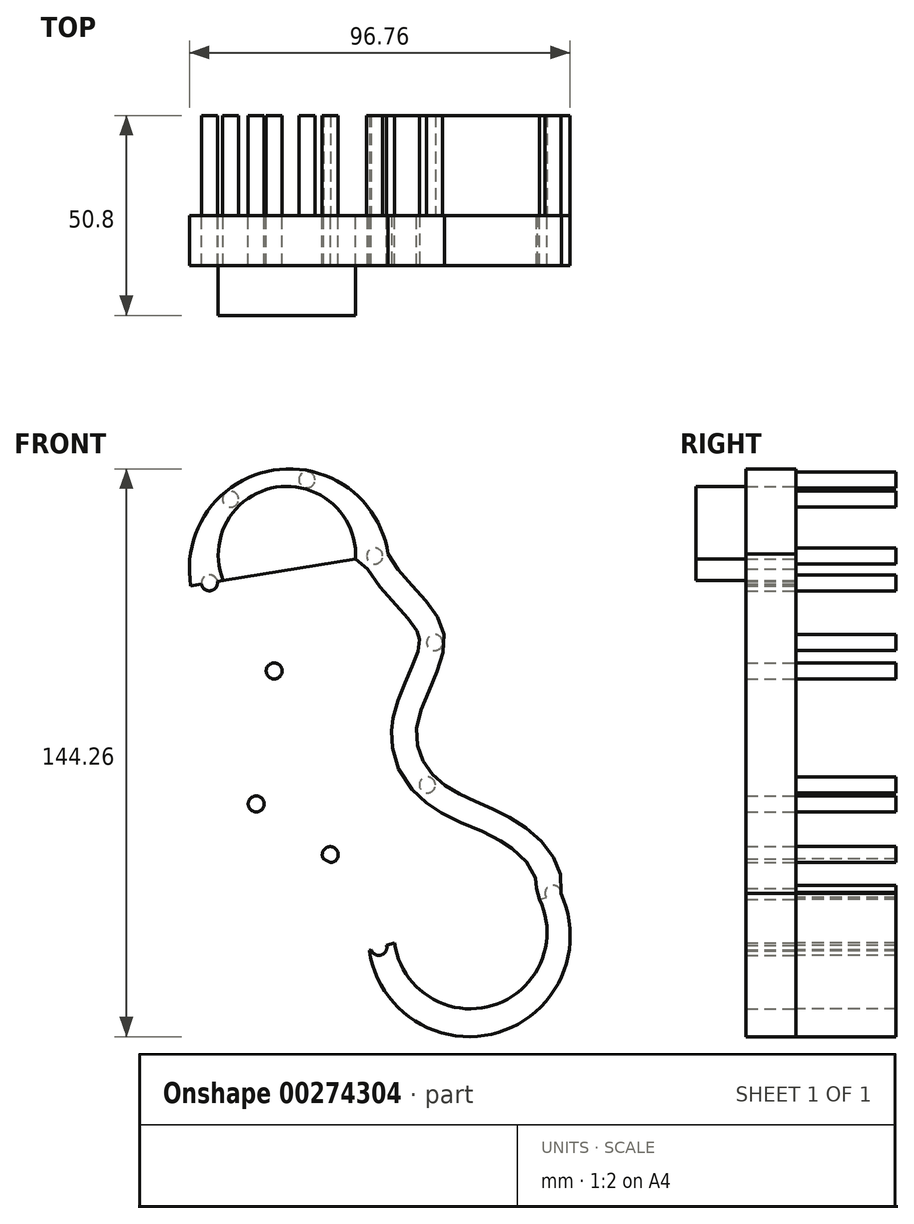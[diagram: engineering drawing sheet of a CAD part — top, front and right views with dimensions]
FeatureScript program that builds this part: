
annotation { "Feature Type Name" : "Feature", "Feature Type Description" : "" }
export const myFeature = defineFeature(function(context is Context, id is Id, definition is map)
    precondition{}
    {
        {
            var Q0;
            Q0=qCreatedBy(makeId("Front.planeOp"),FACE);
            var sketch = newSketch(context, id + "F0", { "sketchPlane" : qUnion([Q0])});
            skLineSegment(sketch, "E0", {"start": v(-45.2, 59.94) * mm, "end": v(4.95, 68.07) * mm});
            skArc(sketch, "E1", {"start": v(4.95, 68.07) * mm, "mid": v(-24.22, 89.33) * mm, "end": v(-45.2, 59.94) * mm});
            skLineSegment(sketch, "E2", {"start": v(0.14, -32.66) * mm, "end": v(48.83, -18.16) * mm});
            skFitSpline(sketch, "E3", {"points": [v(48.83, -18.16) * mm, v(37.71, 0) * mm, v(19, 9.5) * mm, v(12.27, 24.35) * mm, v(19.1, 47.9) * mm, v(4.95, 68.07) * mm], "startDerivative": vector(21.83, 107.44) * mm, "endDerivative": vector(-42.64, 94.14) * mm});
            skArc(sketch, "E4", {"start": v(0.14, -32.66) * mm, "mid": v(32.86, -53.53) * mm, "end": v(48.83, -18.16) * mm});
            skFitSpline(sketch, "E5.0", {"points": [v(-45.21, 59.96) * mm, v(-44.08, 58.98) * mm, v(-41.8, 57.02) * mm, v(-38.45, 54.02) * mm, v(-35.25, 50.94) * mm, v(-32.33, 47.77) * mm, v(-30.2, 45) * mm, v(-28.77, 42.66) * mm, v(-27.85, 40.83) * mm, v(-27.23, 39.23) * mm, v(-26.84, 37.9) * mm, v(-26.53, 36.55) * mm, v(-26.31, 34.87) * mm, v(-26.29, 32.9) * mm, v(-26.46, 30.99) * mm, v(-26.88, 28.53) * mm, v(-27.69, 25.6) * mm, v(-28.86, 22.23) * mm, v(-29.87, 19.47) * mm, v(-30.6, 17.28) * mm, v(-31.28, 15.1) * mm, v(-31.98, 12.3) * mm, v(-32.49, 9.06) * mm, v(-32.56, 6.55) * mm, v(-32.38, 4.74) * mm, v(-32.14, 3.5) * mm, v(-31.79, 2.38) * mm, v(-31.4, 1.55) * mm, v(-31.04, 0.93) * mm, v(-30.73, 0.49) * mm, v(-30.4, 0.06) * mm, v(-29.89, -0.48) * mm, v(-29.08, -1.19) * mm, v(-27.86, -2.05) * mm, v(-26.4, -2.9) * mm, v(-24.2, -4.02) * mm, v(-21.05, -5.38) * mm, v(-16.95, -7) * mm, v(-13.48, -8.46) * mm, v(-10.78, -9.8) * mm, v(-8.81, -10.9) * mm, v(-7.25, -11.96) * mm, v(-6.06, -12.9) * mm, v(-5.34, -13.55) * mm, v(-4.8, -14.1) * mm, v(-4.27, -14.66) * mm, v(-3.66, -15.39) * mm, v(-3, -16.3) * mm, v(-2.22, -17.54) * mm, v(-1.42, -19.16) * mm, v(-0.71, -21.15) * mm, v(-0.23, -23.16) * mm, v(0.17, -25.83) * mm, v(0.3, -29.16) * mm, v(0.14, -33.07) * mm, v(-0.07, -35.6) * mm, v(-0.17, -36.84) * mm]});
            skLineSegment(sketch, "E6", {"start": v(35.15, -22.23) * mm, "end": v(15.07, -28.21) * mm});
            skFitSpline(sketch, "E7.0", {"points": [v(42.6, -16.9) * mm, v(42.65, -16.66) * mm, v(42.7, -16.2) * mm, v(42.69, -15.5) * mm, v(42.56, -14.72) * mm, v(42.2, -13.58) * mm, v(41.39, -11.96) * mm, v(39.8, -9.87) * mm, v(38.05, -8.16) * mm, v(36.5, -6.88) * mm, v(35.47, -6.13) * mm, v(34.63, -5.57) * mm, v(33.8, -5.03) * mm, v(32.28, -4.15) * mm, v(29.98, -3) * mm, v(27.05, -1.72) * mm, v(23.96, -0.42) * mm, v(21.28, 0.78) * mm, v(19.1, 1.9) * mm, v(17.47, 2.84) * mm, v(15.84, 3.9) * mm, v(14.24, 5.13) * mm, v(12.73, 6.47) * mm, v(10.86, 8.44) * mm, v(8.8, 11.2) * mm, v(7.23, 14.39) * mm, v(6.36, 17.16) * mm, v(5.93, 19.34) * mm, v(5.76, 21.21) * mm, v(5.76, 22.74) * mm, v(5.82, 23.9) * mm, v(5.92, 24.87) * mm, v(6.04, 25.65) * mm, v(6.25, 26.8) * mm, v(6.65, 28.45) * mm, v(7.32, 30.53) * mm, v(8.08, 32.51) * mm, v(8.88, 34.41) * mm, v(9.68, 36.23) * mm, v(10.46, 37.97) * mm, v(11.17, 39.63) * mm, v(11.8, 41.18) * mm, v(12.3, 42.62) * mm, v(12.66, 43.9) * mm, v(12.87, 45.02) * mm, v(12.92, 45.78) * mm, v(12.91, 46.28) * mm, v(12.88, 46.6) * mm, v(12.83, 46.9) * mm, v(12.75, 47.22) * mm, v(12.62, 47.58) * mm, v(12.4, 48.12) * mm, v(12, 48.9) * mm, v(11.3, 49.98) * mm, v(10.4, 51.16) * mm, v(9.35, 52.42) * mm, v(8.17, 53.75) * mm, v(6.46, 55.6) * mm, v(4.17, 58.07) * mm, v(1.9, 60.82) * mm, v(0.24, 63.33) * mm, v(-0.5, 64.71) * mm, v(-0.83, 65.45) * mm]});
            skFitSpline(sketch, "E8.0", {"points": [v(-41.07, 64.76) * mm, v(-39.94, 63.8) * mm, v(-37.63, 61.8) * mm, v(-34.15, 58.69) * mm, v(-31.3, 55.96) * mm, v(-29.1, 53.65) * mm, v(-27.52, 51.84) * mm, v(-26, 49.95) * mm, v(-24.56, 47.93) * mm, v(-23.23, 45.77) * mm, v(-22.24, 43.82) * mm, v(-21.55, 42.16) * mm, v(-21.09, 40.87) * mm, v(-20.69, 39.51) * mm, v(-20.37, 38.1) * mm, v(-20.14, 36.7) * mm, v(-19.96, 34.86) * mm, v(-19.93, 32.65) * mm, v(-20.15, 30.15) * mm, v(-20.55, 27.85) * mm, v(-21.07, 25.7) * mm, v(-21.65, 23.7) * mm, v(-22.27, 21.85) * mm, v(-22.9, 20.09) * mm, v(-23.5, 18.42) * mm, v(-24.06, 16.84) * mm, v(-24.56, 15.33) * mm, v(-25.01, 13.87) * mm, v(-25.4, 12.44) * mm, v(-25.72, 11.04) * mm, v(-25.95, 9.71) * mm, v(-26.1, 8.48) * mm, v(-26.18, 7.37) * mm, v(-26.16, 6.41) * mm, v(-26.09, 5.63) * mm, v(-25.97, 5.05) * mm, v(-25.84, 4.65) * mm, v(-25.74, 4.46) * mm, v(-25.68, 4.35) * mm, v(-25.64, 4.28) * mm, v(-25.59, 4.22) * mm, v(-25.53, 4.16) * mm, v(-25.38, 4.02) * mm, v(-25.06, 3.76) * mm, v(-24.45, 3.32) * mm, v(-23.38, 2.69) * mm, v(-22.02, 2) * mm, v(-20.4, 1.26) * mm, v(-18.6, 0.5) * mm, v(-16.64, -0.3) * mm, v(-14.55, -1.14) * mm, v(-12.38, -2.04) * mm, v(-10.13, -3.04) * mm, v(-7.83, -4.16) * mm, v(-5.89, -5.26) * mm, v(-4.31, -6.27) * mm, v(-3.13, -7.12) * mm, v(-2.15, -7.9) * mm, v(-1.37, -8.57) * mm, v(-0.8, -9.11) * mm, v(-0.22, -9.68) * mm, v(0.5, -10.46) * mm, v(1.35, -11.48) * mm, v(2.27, -12.74) * mm, v(3.35, -14.48) * mm, v(4.45, -16.7) * mm, v(5.39, -19.36) * mm, v(6.01, -21.96) * mm, v(6.38, -24.46) * mm, v(6.57, -26.86) * mm, v(6.63, -29.93) * mm, v(6.48, -33.51) * mm, v(6.26, -36.13) * mm, v(6.15, -37.37) * mm]});
            skLineSegment(sketch, "E9", {"start": v(-0.23, 64.22) * mm, "end": v(-3.34, 66.72) * mm});
            skLineSegment(sketch, "E10", {"start": v(42.6, -16.9) * mm, "end": v(43.46, -19.76) * mm});
            skLineSegment(sketch, "E11", {"start": v(6.58, -30.8) * mm, "end": v(8.9, -30.05) * mm});
            skLineSegment(sketch, "E12", {"start": v(-36.93, 61.17) * mm, "end": v(-32.97, 61.92) * mm});
            skCircle(sketch, "E13", {"center": v(46.85, -18.16) * mm, "radius": 2.03 * mm});
            skCircle(sketch, "E14", {"center": v(38.49, -49.03) * mm, "radius": 2.03 * mm});
            skCircle(sketch, "E15", {"center": v(14.6, -49.33) * mm, "radius": 2.03 * mm});
            skCircle(sketch, "E16", {"center": v(2.6, -31.93) * mm, "radius": 2.03 * mm});
            skCircle(sketch, "E17", {"center": v(-9.75, -8.35) * mm, "radius": 2.03 * mm});
            skCircle(sketch, "E18", {"center": v(14.9, 9.35) * mm, "radius": 2.03 * mm});
            skCircle(sketch, "E19", {"center": v(-28.57, 4.54) * mm, "radius": 2.03 * mm});
            skCircle(sketch, "E20", {"center": v(16.77, 45.53) * mm, "radius": 2.03 * mm});
            skCircle(sketch, "E21", {"center": v(-24.01, 38.33) * mm, "radius": 2.03 * mm});
            skCircle(sketch, "E22", {"center": v(-40.44, 60.7) * mm, "radius": 2.03 * mm});
            skCircle(sketch, "E23", {"center": v(1.55, 67.51) * mm, "radius": 2.03 * mm});
            skCircle(sketch, "E24", {"center": v(-35.08, 81.96) * mm, "radius": 2.03 * mm});
            skCircle(sketch, "E25", {"center": v(-15.68, 86.88) * mm, "radius": 2.03 * mm});
            skArc(sketch, "E26", {"start": v(6.58, -30.8) * mm, "mid": v(31.44, -46.7) * mm, "end": v(43.46, -19.76) * mm});
            skArc(sketch, "E27", {"start": v(-3.34, 66.72) * mm, "mid": v(-23.61, 84.97) * mm, "end": v(-36.93, 61.17) * mm});
            skSolve(sketch);
        }
        {
            var Q0;
            {var subQ1=sQuery(id+"F0.wireOp",EDGE,"E6");Q0=makeQuery(id+"F0.imprint","IMPRINT",FACE,{"disambiguationData":[TD([[makeQuery(id+"F0.imprint","IMPRINT",EDGE,{"derivedFrom":subQ1}),1.0]])]});}
            var Q1;
            {var subQ0=sQuery(id+"F0.wireOp",EDGE,"E6");Q1=makeQuery(id+"F0.imprint","IMPRINT",FACE,{"disambiguationData":[TD([[makeQuery(id+"F0.imprint","IMPRINT",EDGE,{"derivedFrom":subQ0}),-1.0]])]});}
            var Q2;
            {var subQ0=sQuery(id+"F0.wireOp",EDGE,"E0");var subQ1=makeQuery(id+"F0.imprint","INTERSECT",VERTEX,{"derivedFrom":[subQ0,sQuery(id+"F0.wireOp",EDGE,"E12")]});Q2=makeQuery(id+"F0.imprint","IMPRINT",FACE,{"disambiguationData":[TD([[makeQuery(id+"F0.imprint","IMPRINT",EDGE,{"disambiguationData":[TD([[subQ1,1.0]])],"derivedFrom":subQ0}),1.0]])]});}
            extrude(context, id + "F1", {"entities" : qUnion([Q0, Q1, Q2]), "depth" : 25.4 * mm});
        }
        {
            var Q0;
            {var subQ0=sQuery(id+"F0.wireOp",EDGE,"E14");var subQ1=sQuery(id+"F0.wireOp",EDGE,"E4");var subQ2=makeQuery(id+"F0.imprint","INTERSECT",VERTEX,{"disambiguationData":[OD(0.0)],"derivedFrom":[subQ1,subQ0]});Q0=makeQuery(id+"F0.imprint","IMPRINT",FACE,{"disambiguationData":[TD([[makeQuery(id+"F0.imprint","IMPRINT",EDGE,{"disambiguationData":[TD([[subQ2,-1.0]])],"derivedFrom":subQ1}),1.0]])]});}
            var Q1;
            {var subQ0=sQuery(id+"F0.wireOp",EDGE,"E3");var subQ3=sQuery(id+"F0.wireOp",EDGE,"E13");var subQ5=makeQuery(id+"F0.imprint","INTERSECT",VERTEX,{"derivedFrom":[subQ0,subQ3]});Q1=makeQuery(id+"F0.imprint","IMPRINT",FACE,{"disambiguationData":[TD([[makeQuery(id+"F0.imprint","IMPRINT",EDGE,{"disambiguationData":[TD([[subQ5,-1.0]])],"derivedFrom":subQ3}),1.0]])]});}
            var Q2;
            {var subQ0=sQuery(id+"F0.wireOp",EDGE,"E4");var subQ3=sQuery(id+"F0.wireOp",EDGE,"E13");var subQ5=makeQuery(id+"F0.imprint","INTERSECT",VERTEX,{"derivedFrom":[subQ0,subQ3]});Q2=makeQuery(id+"F0.imprint","IMPRINT",FACE,{"disambiguationData":[TD([[makeQuery(id+"F0.imprint","IMPRINT",EDGE,{"disambiguationData":[TD([[subQ5,1.0]])],"derivedFrom":subQ3}),1.0]])]});}
            var Q3;
            {var subQ0=sQuery(id+"F0.wireOp",EDGE,"E16");var subQ1=sQuery(id+"F0.wireOp",EDGE,"E2");var subQ2=makeQuery(id+"F0.imprint","INTERSECT",VERTEX,{"disambiguationData":[OD(0.0)],"derivedFrom":[subQ1,subQ0]});Q3=makeQuery(id+"F0.imprint","IMPRINT",FACE,{"disambiguationData":[TD([[makeQuery(id+"F0.imprint","IMPRINT",EDGE,{"disambiguationData":[TD([[subQ2,-1.0]])],"derivedFrom":subQ1}),-1.0]])]});}
            var Q4;
            {var subQ0=sQuery(id+"F0.wireOp",EDGE,"E16");var subQ1=sQuery(id+"F0.wireOp",EDGE,"E2");var subQ2=makeQuery(id+"F0.imprint","INTERSECT",VERTEX,{"disambiguationData":[OD(0.0)],"derivedFrom":[subQ1,subQ0]});Q4=makeQuery(id+"F0.imprint","IMPRINT",FACE,{"disambiguationData":[TD([[makeQuery(id+"F0.imprint","IMPRINT",EDGE,{"disambiguationData":[TD([[subQ2,-1.0]])],"derivedFrom":subQ1}),1.0]])]});}
            var Q5;
            Q5=makeQuery(id+"F0.imprint","IMPRINT",FACE,{"disambiguationData":[TD([[makeQuery(id+"F0.imprint","IMPRINT",EDGE,{"derivedFrom":sQuery(id+"F0.wireOp",EDGE,"E15")}),1.0]])]});
            var Q6;
            {var subQ0=sQuery(id+"F0.wireOp",EDGE,"E17");var subQ1=sQuery(id+"F0.wireOp",EDGE,"E5.0");var subQ2=makeQuery(id+"F0.imprint","INTERSECT",VERTEX,{"disambiguationData":[OD(0.0)],"derivedFrom":[subQ1,subQ0]});Q6=makeQuery(id+"F0.imprint","IMPRINT",FACE,{"disambiguationData":[TD([[makeQuery(id+"F0.imprint","IMPRINT",EDGE,{"disambiguationData":[TD([[subQ2,-1.0]])],"derivedFrom":subQ1}),1.0]])]});}
            var Q7;
            Q7=makeQuery(id+"F0.imprint","IMPRINT",FACE,{"disambiguationData":[TD([[makeQuery(id+"F0.imprint","IMPRINT",EDGE,{"derivedFrom":sQuery(id+"F0.wireOp",EDGE,"E18")}),1.0]])]});
            var Q8;
            Q8=makeQuery(id+"F0.imprint","IMPRINT",FACE,{"disambiguationData":[TD([[makeQuery(id+"F0.imprint","IMPRINT",EDGE,{"derivedFrom":sQuery(id+"F0.wireOp",EDGE,"E20")}),1.0]])]});
            var Q9;
            Q9=makeQuery(id+"F0.imprint","IMPRINT",FACE,{"disambiguationData":[TD([[makeQuery(id+"F0.imprint","IMPRINT",EDGE,{"derivedFrom":sQuery(id+"F0.wireOp",EDGE,"E19")}),1.0]])]});
            var Q10;
            {var subQ0=sQuery(id+"F0.wireOp",EDGE,"E23");var subQ1=sQuery(id+"F0.wireOp",EDGE,"E0");var subQ2=makeQuery(id+"F0.imprint","INTERSECT",VERTEX,{"disambiguationData":[OD(0.0)],"derivedFrom":[subQ1,subQ0]});Q10=makeQuery(id+"F0.imprint","IMPRINT",FACE,{"disambiguationData":[TD([[makeQuery(id+"F0.imprint","IMPRINT",EDGE,{"disambiguationData":[TD([[subQ2,-1.0]])],"derivedFrom":subQ1}),-1.0]])]});}
            var Q11;
            {var subQ0=sQuery(id+"F0.wireOp",EDGE,"E23");var subQ1=sQuery(id+"F0.wireOp",EDGE,"E0");var subQ2=makeQuery(id+"F0.imprint","INTERSECT",VERTEX,{"disambiguationData":[OD(0.0)],"derivedFrom":[subQ1,subQ0]});Q11=makeQuery(id+"F0.imprint","IMPRINT",FACE,{"disambiguationData":[TD([[makeQuery(id+"F0.imprint","IMPRINT",EDGE,{"disambiguationData":[TD([[subQ2,-1.0]])],"derivedFrom":subQ1}),1.0]])]});}
            var Q12;
            Q12=makeQuery(id+"F0.imprint","IMPRINT",FACE,{"disambiguationData":[TD([[makeQuery(id+"F0.imprint","IMPRINT",EDGE,{"derivedFrom":sQuery(id+"F0.wireOp",EDGE,"E21")}),1.0]])]});
            var Q13;
            Q13=makeQuery(id+"F0.imprint","IMPRINT",FACE,{"disambiguationData":[TD([[makeQuery(id+"F0.imprint","IMPRINT",EDGE,{"derivedFrom":sQuery(id+"F0.wireOp",EDGE,"E25")}),1.0]])]});
            var Q14;
            Q14=makeQuery(id+"F0.imprint","IMPRINT",FACE,{"disambiguationData":[TD([[makeQuery(id+"F0.imprint","IMPRINT",EDGE,{"derivedFrom":sQuery(id+"F0.wireOp",EDGE,"E24")}),1.0]])]});
            var Q15;
            {var subQ0=sQuery(id+"F0.wireOp",EDGE,"E22");var subQ1=sQuery(id+"F0.wireOp",EDGE,"E0");var subQ2=makeQuery(id+"F0.imprint","INTERSECT",VERTEX,{"disambiguationData":[OD(0.0)],"derivedFrom":[subQ1,subQ0]});Q15=makeQuery(id+"F0.imprint","IMPRINT",FACE,{"disambiguationData":[TD([[makeQuery(id+"F0.imprint","IMPRINT",EDGE,{"disambiguationData":[TD([[subQ2,-1.0]])],"derivedFrom":subQ1}),1.0]])]});}
            var Q16;
            {var subQ0=sQuery(id+"F0.wireOp",EDGE,"E22");var subQ1=sQuery(id+"F0.wireOp",EDGE,"E0");var subQ2=makeQuery(id+"F0.imprint","INTERSECT",VERTEX,{"disambiguationData":[OD(0.0)],"derivedFrom":[subQ1,subQ0]});Q16=makeQuery(id+"F0.imprint","IMPRINT",FACE,{"disambiguationData":[TD([[makeQuery(id+"F0.imprint","IMPRINT",EDGE,{"disambiguationData":[TD([[subQ2,-1.0]])],"derivedFrom":subQ1}),-1.0]])]});}
            extrude(context, id + "F2", {"entities" : qUnion([Q0, Q1, Q2, Q3, Q4, Q5, Q6, Q7, Q8, Q9, Q10, Q11, Q12, Q13, Q14, Q15, Q16]), "oppositeDirection" : true, "depth" : 25.4 * mm});
        }
        {
            var Q0;
            Q0=makeQuery(id+"F0.imprint","IMPRINT",FACE,{"disambiguationData":[TD([[makeQuery(id+"F0.imprint","IMPRINT",EDGE,{"derivedFrom":sQuery(id+"F0.wireOp",EDGE,"E19")}),-1.0]])]});
            var Q1;
            {var subQ0=sQuery(id+"F0.wireOp",EDGE,"E1");Q1=makeQuery(id+"F0.imprint","IMPRINT",FACE,{"disambiguationData":[TD([[makeQuery(id+"F0.imprint","IMPRINT",EDGE,{"derivedFrom":subQ0}),1.0]])]});}
            var Q2;
            Q2=makeQuery(id+"F0.imprint","IMPRINT",FACE,{"disambiguationData":[TD([[makeQuery(id+"F0.imprint","IMPRINT",EDGE,{"derivedFrom":sQuery(id+"F0.wireOp",EDGE,"E15")}),-1.0]])]});
            var Q3;
            {var subQ0=sQuery(id+"F0.wireOp",EDGE,"E4");var subQ3=sQuery(id+"F0.wireOp",EDGE,"E13");var subQ5=makeQuery(id+"F0.imprint","INTERSECT",VERTEX,{"derivedFrom":[subQ0,subQ3]});Q3=makeQuery(id+"F0.imprint","IMPRINT",FACE,{"disambiguationData":[TD([[makeQuery(id+"F0.imprint","IMPRINT",EDGE,{"disambiguationData":[TD([[subQ5,1.0]])],"derivedFrom":subQ3}),1.0]])]});}
            var Q4;
            {var subQ0=sQuery(id+"F0.wireOp",EDGE,"E3");var subQ3=sQuery(id+"F0.wireOp",EDGE,"E13");var subQ5=makeQuery(id+"F0.imprint","INTERSECT",VERTEX,{"derivedFrom":[subQ0,subQ3]});Q4=makeQuery(id+"F0.imprint","IMPRINT",FACE,{"disambiguationData":[TD([[makeQuery(id+"F0.imprint","IMPRINT",EDGE,{"disambiguationData":[TD([[subQ5,-1.0]])],"derivedFrom":subQ3}),1.0]])]});}
            var Q5;
            Q5=makeQuery(id+"F0.imprint","IMPRINT",FACE,{"disambiguationData":[TD([[makeQuery(id+"F0.imprint","IMPRINT",EDGE,{"derivedFrom":sQuery(id+"F0.wireOp",EDGE,"E7.0")}),-1.0]])]});
            var Q6;
            {var subQ0=sQuery(id+"F0.wireOp",EDGE,"E14");var subQ1=sQuery(id+"F0.wireOp",EDGE,"E4");var subQ2=makeQuery(id+"F0.imprint","INTERSECT",VERTEX,{"disambiguationData":[OD(0.0)],"derivedFrom":[subQ1,subQ0]});Q6=makeQuery(id+"F0.imprint","IMPRINT",FACE,{"disambiguationData":[TD([[makeQuery(id+"F0.imprint","IMPRINT",EDGE,{"disambiguationData":[TD([[subQ2,-1.0]])],"derivedFrom":subQ1}),1.0]])]});}
            var Q7;
            Q7=makeQuery(id+"F0.imprint","IMPRINT",FACE,{"disambiguationData":[TD([[makeQuery(id+"F0.imprint","IMPRINT",EDGE,{"derivedFrom":sQuery(id+"F0.wireOp",EDGE,"E15")}),1.0]])]});
            var Q8;
            {var subQ0=sQuery(id+"F0.wireOp",EDGE,"E16");var subQ1=sQuery(id+"F0.wireOp",EDGE,"E2");var subQ2=makeQuery(id+"F0.imprint","INTERSECT",VERTEX,{"disambiguationData":[OD(0.0)],"derivedFrom":[subQ1,subQ0]});Q8=makeQuery(id+"F0.imprint","IMPRINT",FACE,{"disambiguationData":[TD([[makeQuery(id+"F0.imprint","IMPRINT",EDGE,{"disambiguationData":[TD([[subQ2,-1.0]])],"derivedFrom":subQ1}),1.0]])]});}
            var Q9;
            {var subQ0=sQuery(id+"F0.wireOp",EDGE,"E16");var subQ1=sQuery(id+"F0.wireOp",EDGE,"E2");var subQ2=makeQuery(id+"F0.imprint","INTERSECT",VERTEX,{"disambiguationData":[OD(0.0)],"derivedFrom":[subQ1,subQ0]});Q9=makeQuery(id+"F0.imprint","IMPRINT",FACE,{"disambiguationData":[TD([[makeQuery(id+"F0.imprint","IMPRINT",EDGE,{"disambiguationData":[TD([[subQ2,-1.0]])],"derivedFrom":subQ1}),-1.0]])]});}
            var Q10;
            {var subQ0=sQuery(id+"F0.wireOp",EDGE,"E17");var subQ1=sQuery(id+"F0.wireOp",EDGE,"E5.0");var subQ2=makeQuery(id+"F0.imprint","INTERSECT",VERTEX,{"disambiguationData":[OD(0.0)],"derivedFrom":[subQ1,subQ0]});Q10=makeQuery(id+"F0.imprint","IMPRINT",FACE,{"disambiguationData":[TD([[makeQuery(id+"F0.imprint","IMPRINT",EDGE,{"disambiguationData":[TD([[subQ2,-1.0]])],"derivedFrom":subQ1}),1.0]])]});}
            var Q11;
            Q11=makeQuery(id+"F0.imprint","IMPRINT",FACE,{"disambiguationData":[TD([[makeQuery(id+"F0.imprint","IMPRINT",EDGE,{"derivedFrom":sQuery(id+"F0.wireOp",EDGE,"E18")}),1.0]])]});
            var Q12;
            Q12=makeQuery(id+"F0.imprint","IMPRINT",FACE,{"disambiguationData":[TD([[makeQuery(id+"F0.imprint","IMPRINT",EDGE,{"derivedFrom":sQuery(id+"F0.wireOp",EDGE,"E20")}),1.0]])]});
            var Q13;
            Q13=makeQuery(id+"F0.imprint","IMPRINT",FACE,{"disambiguationData":[TD([[makeQuery(id+"F0.imprint","IMPRINT",EDGE,{"derivedFrom":sQuery(id+"F0.wireOp",EDGE,"E21")}),1.0]])]});
            var Q14;
            Q14=makeQuery(id+"F0.imprint","IMPRINT",FACE,{"disambiguationData":[TD([[makeQuery(id+"F0.imprint","IMPRINT",EDGE,{"derivedFrom":sQuery(id+"F0.wireOp",EDGE,"E19")}),1.0]])]});
            var Q15;
            {var subQ0=sQuery(id+"F0.wireOp",EDGE,"E23");var subQ1=sQuery(id+"F0.wireOp",EDGE,"E0");var subQ2=makeQuery(id+"F0.imprint","INTERSECT",VERTEX,{"disambiguationData":[OD(0.0)],"derivedFrom":[subQ1,subQ0]});Q15=makeQuery(id+"F0.imprint","IMPRINT",FACE,{"disambiguationData":[TD([[makeQuery(id+"F0.imprint","IMPRINT",EDGE,{"disambiguationData":[TD([[subQ2,-1.0]])],"derivedFrom":subQ1}),1.0]])]});}
            var Q16;
            {var subQ0=sQuery(id+"F0.wireOp",EDGE,"E23");var subQ1=sQuery(id+"F0.wireOp",EDGE,"E0");var subQ2=makeQuery(id+"F0.imprint","INTERSECT",VERTEX,{"disambiguationData":[OD(0.0)],"derivedFrom":[subQ1,subQ0]});Q16=makeQuery(id+"F0.imprint","IMPRINT",FACE,{"disambiguationData":[TD([[makeQuery(id+"F0.imprint","IMPRINT",EDGE,{"disambiguationData":[TD([[subQ2,-1.0]])],"derivedFrom":subQ1}),-1.0]])]});}
            var Q17;
            Q17=makeQuery(id+"F0.imprint","IMPRINT",FACE,{"disambiguationData":[TD([[makeQuery(id+"F0.imprint","IMPRINT",EDGE,{"derivedFrom":sQuery(id+"F0.wireOp",EDGE,"E25")}),1.0]])]});
            var Q18;
            Q18=makeQuery(id+"F0.imprint","IMPRINT",FACE,{"disambiguationData":[TD([[makeQuery(id+"F0.imprint","IMPRINT",EDGE,{"derivedFrom":sQuery(id+"F0.wireOp",EDGE,"E24")}),1.0]])]});
            var Q19;
            {var subQ0=sQuery(id+"F0.wireOp",EDGE,"E22");var subQ1=sQuery(id+"F0.wireOp",EDGE,"E0");var subQ2=makeQuery(id+"F0.imprint","INTERSECT",VERTEX,{"disambiguationData":[OD(0.0)],"derivedFrom":[subQ1,subQ0]});Q19=makeQuery(id+"F0.imprint","IMPRINT",FACE,{"disambiguationData":[TD([[makeQuery(id+"F0.imprint","IMPRINT",EDGE,{"disambiguationData":[TD([[subQ2,-1.0]])],"derivedFrom":subQ1}),1.0]])]});}
            var Q20;
            {var subQ0=sQuery(id+"F0.wireOp",EDGE,"E22");var subQ1=sQuery(id+"F0.wireOp",EDGE,"E0");var subQ2=makeQuery(id+"F0.imprint","INTERSECT",VERTEX,{"disambiguationData":[OD(0.0)],"derivedFrom":[subQ1,subQ0]});Q20=makeQuery(id+"F0.imprint","IMPRINT",FACE,{"disambiguationData":[TD([[makeQuery(id+"F0.imprint","IMPRINT",EDGE,{"disambiguationData":[TD([[subQ2,-1.0]])],"derivedFrom":subQ1}),-1.0]])]});}
            extrude(context, id + "F3", {"entities" : qUnion([Q0, Q1, Q2, Q3, Q4, Q5, Q6, Q7, Q8, Q9, Q10, Q11, Q12, Q13, Q14, Q15, Q16, Q17, Q18, Q19, Q20]), "depth" : 12.7 * mm});
        }
    });
